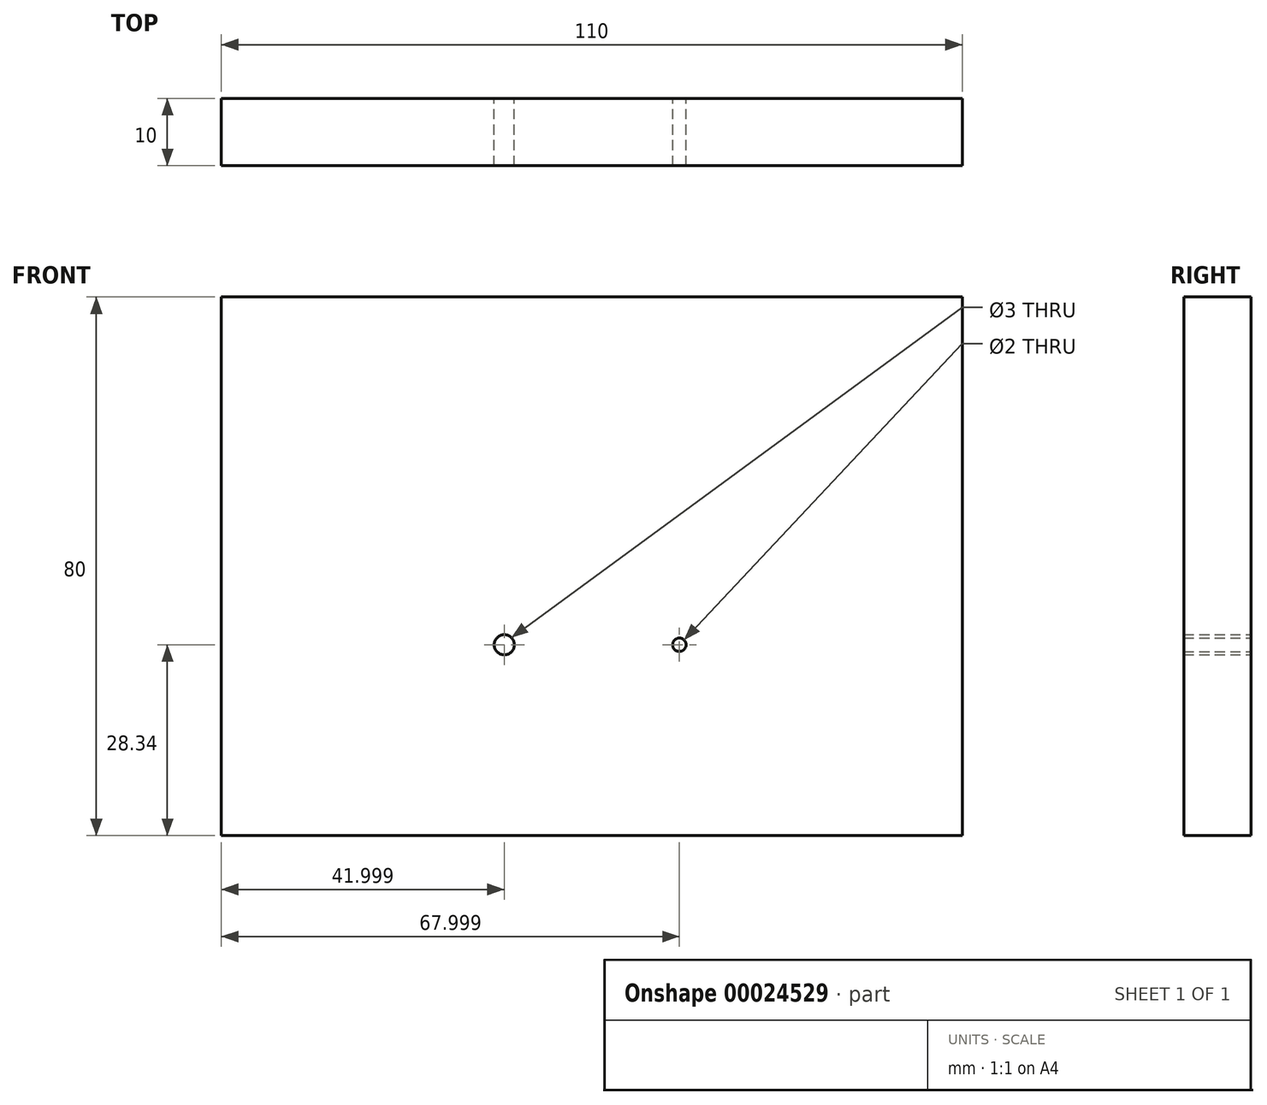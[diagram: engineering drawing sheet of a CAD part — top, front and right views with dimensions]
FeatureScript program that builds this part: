
annotation { "Feature Type Name" : "Feature", "Feature Type Description" : "" }
export const myFeature = defineFeature(function(context is Context, id is Id, definition is map)
    precondition{}
    {
        {
            var Q0;
            Q0=qCreatedBy(makeId("Front.planeOp"),FACE);
            var sketch = newSketch(context, id + "F0", { "sketchPlane" : qUnion([Q0])});
            skLineSegment(sketch, "E0", {"start": v(-110.8, 31.1) * mm, "end": v(-110.8, -48.9) * mm});
            skLineSegment(sketch, "E1", {"start": v(-110.8, -48.9) * mm, "end": v(-0.8, -48.9) * mm});
            skLineSegment(sketch, "E2", {"start": v(-0.8, -48.9) * mm, "end": v(-0.8, 31.1) * mm});
            skLineSegment(sketch, "E3", {"start": v(-0.8, 31.1) * mm, "end": v(-110.8, 31.1) * mm});
            skCircle(sketch, "E4", {"center": v(-68.8, -20.57) * mm, "radius": 1.5 * mm});
            skCircle(sketch, "E5", {"center": v(-42.8, -20.57) * mm, "radius": 1 * mm});
            skSolve(sketch);
        }
        {
            var Q0;
            Q0=makeQuery(id+"F0.imprint","IMPRINT",FACE,{"disambiguationData":[TD([[makeQuery(id+"F0.imprint","IMPRINT",EDGE,{"derivedFrom":sQuery(id+"F0.wireOp",EDGE,"E0")}),1.0]])]});
            extrude(context, id + "F1", {"entities" : qUnion([Q0]), "depth" : 10 * mm});
        }
    });
